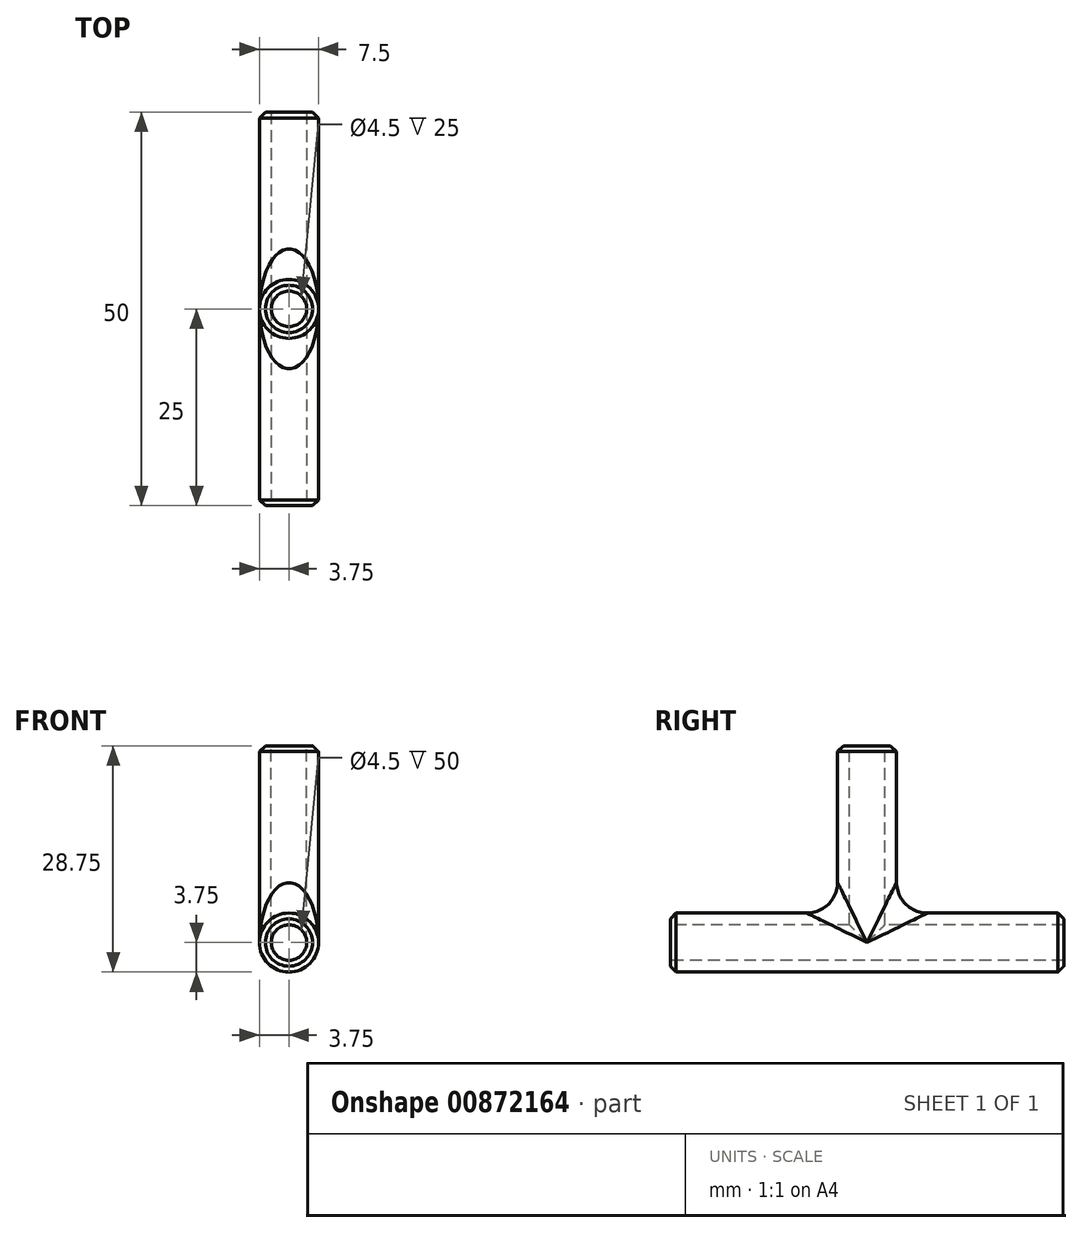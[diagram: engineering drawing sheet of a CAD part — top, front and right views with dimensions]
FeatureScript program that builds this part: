
annotation { "Feature Type Name" : "Feature", "Feature Type Description" : "" }
export const myFeature = defineFeature(function(context is Context, id is Id, definition is map)
    precondition{}
    {
        {
            var Q0;
            Q0=qCreatedBy(makeId("Front.planeOp"),FACE);
            var sketch = newSketch(context, id + "F0", { "sketchPlane" : qUnion([Q0])});
            skCircle(sketch, "E0", {"center": v(0, 0) * mm, "radius": 3.75 * mm});
            skSolve(sketch);
        }
        {
            var Q0;
            Q0 = qSketchRegion(id + "F0", true);
            extrude(context, id + "F1", {"entities" : qUnion([Q0]), "endBound" : BoundingType.SYMMETRIC, "depth" : 50 * mm, "offsetDistance" : 25 * mm});
        }
        {
            var Q0;
            Q0=qCreatedBy(makeId("Top.planeOp"),FACE);
            var sketch = newSketch(context, id + "F2", { "sketchPlane" : qUnion([Q0])});
            skCircle(sketch, "E1", {"center": v(0, 0) * mm, "radius": 3.75 * mm});
            skSolve(sketch);
        }
        {
            var Q0;
            Q0 = qSketchRegion(id + "F2", true);
            extrude(context, id + "F3", {"entities" : qUnion([Q0]), "operationType" : NewBodyOperationType.ADD, "depth" : 25 * mm, "offsetDistance" : 25 * mm});
        }
        {
            var Q0;
            Q0=makeQuery(id+"F1.opExtrude","CAP_FACE",FACE,{"disambiguationData":[OSD([sQuery(id+"F0.wireOp",EDGE,"E0")])],"isStart":false});
            var sketch = newSketch(context, id + "F4", { "sketchPlane" : qUnion([Q0])});
            skCircle(sketch, "E2", {"center": v(0, 0) * mm, "radius": 2.25 * mm});
            skSolve(sketch);
        }
        {
            var Q0;
            Q0 = qSketchRegion(id + "F4", true);
            extrude(context, id + "F5", {"entities" : qUnion([Q0]), "operationType" : NewBodyOperationType.REMOVE, "oppositeDirection" : true, "depth" : 50 * mm, "offsetDistance" : 25 * mm});
        }
        {
            var Q0;
            Q0=makeQuery(id+"F3.opExtrude","CAP_FACE",FACE,{"disambiguationData":[OSD([sQuery(id+"F2.wireOp",EDGE,"E1")])],"isStart":false});
            var sketch = newSketch(context, id + "F6", { "sketchPlane" : qUnion([Q0])});
            skCircle(sketch, "E3", {"center": v(0, 0) * mm, "radius": 2.25 * mm});
            skSolve(sketch);
        }
        {
            var Q0;
            Q0 = qSketchRegion(id + "F6", true);
            extrude(context, id + "F7", {"entities" : qUnion([Q0]), "operationType" : NewBodyOperationType.REMOVE, "oppositeDirection" : true, "depth" : 25 * mm, "offsetDistance" : 25 * mm});
        }
        {
            var Q0;
            Q0=makeQuery(id+"F3.opExtrude","CAP_EDGE",EDGE,{"disambiguationData":[OSD([sQuery(id+"F2.wireOp",EDGE,"E1")])],"isStart":false});
            var Q1;
            Q1=makeQuery(id+"F1.opExtrude","CAP_EDGE",EDGE,{"disambiguationData":[OSD([sQuery(id+"F0.wireOp",EDGE,"E0")])],"isStart":false});
            var Q2;
            Q2=makeQuery(id+"F1.opExtrude","CAP_EDGE",EDGE,{"disambiguationData":[OSD([sQuery(id+"F0.wireOp",EDGE,"E0")])],"isStart":true});
            chamfer(context, id + "F8", {"entities" : qUnion([Q0, Q1, Q2]), "width" : .75 * mm, "tangentPropagation" : true});
        }
        {
            var Q0;
            Q0=makeQuery(id+"F3.boolean.opBoolean","INTERSECT",EDGE,{"disambiguationData":[OD(1.0)],"derivedFrom":[makeQuery(id+"F1.opExtrude","SWEPT_FACE",FACE,{"disambiguationData":[OSD([sQuery(id+"F0.wireOp",EDGE,"E0")])]}),makeQuery(id+"F3.opExtrude","SWEPT_FACE",FACE,{"disambiguationData":[OSD([sQuery(id+"F2.wireOp",EDGE,"E1")])]})]});
            var Q1;
            Q1=makeQuery(id+"F3.boolean.opBoolean","INTERSECT",EDGE,{"disambiguationData":[OD(0.0)],"derivedFrom":[makeQuery(id+"F1.opExtrude","SWEPT_FACE",FACE,{"disambiguationData":[OSD([sQuery(id+"F0.wireOp",EDGE,"E0")])]}),makeQuery(id+"F3.opExtrude","SWEPT_FACE",FACE,{"disambiguationData":[OSD([sQuery(id+"F2.wireOp",EDGE,"E1")])]})]});
            fillet(context, id + "F9", {"entities" : qUnion([Q0, Q1]), "radius" : 3.9 * mm, "tangentPropagation" : true, "allowEdgeOverflow" : false});
        }
    });
